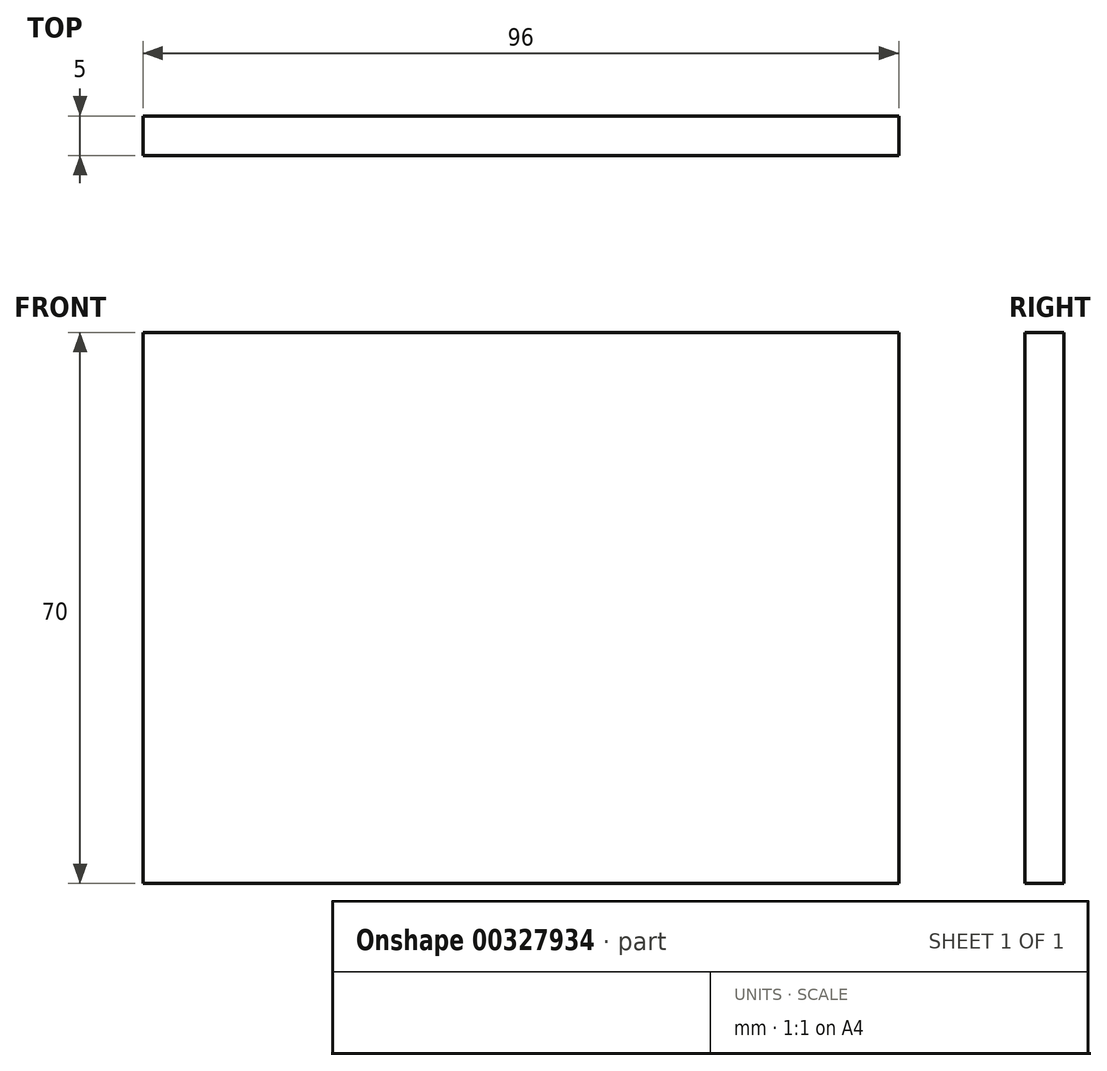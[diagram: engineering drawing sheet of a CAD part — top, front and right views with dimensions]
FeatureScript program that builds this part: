
annotation { "Feature Type Name" : "Feature", "Feature Type Description" : "" }
export const myFeature = defineFeature(function(context is Context, id is Id, definition is map)
    precondition{}
    {
        {
            var Q0;
            Q0=qCreatedBy(makeId("Front.planeOp"),FACE);
            var sketch = newSketch(context, id + "F0", { "sketchPlane" : qUnion([Q0])});
            skLineSegment(sketch, "E0", {"start": v(0, 70) * mm, "end": v(96, 70) * mm});
            skLineSegment(sketch, "E1", {"start": v(96, 70) * mm, "end": v(96, 0) * mm});
            skLineSegment(sketch, "E2", {"start": v(96, 0) * mm, "end": v(0, 0) * mm});
            skLineSegment(sketch, "E3", {"start": v(0, 0) * mm, "end": v(0, 70) * mm});
            skSolve(sketch);
        }
        {
            var Q0;
            Q0 = qSketchRegion(id + "F0", true);
            extrude(context, id + "F1", {"entities" : qUnion([Q0]), "depth" : 5 * mm});
        }
    });
